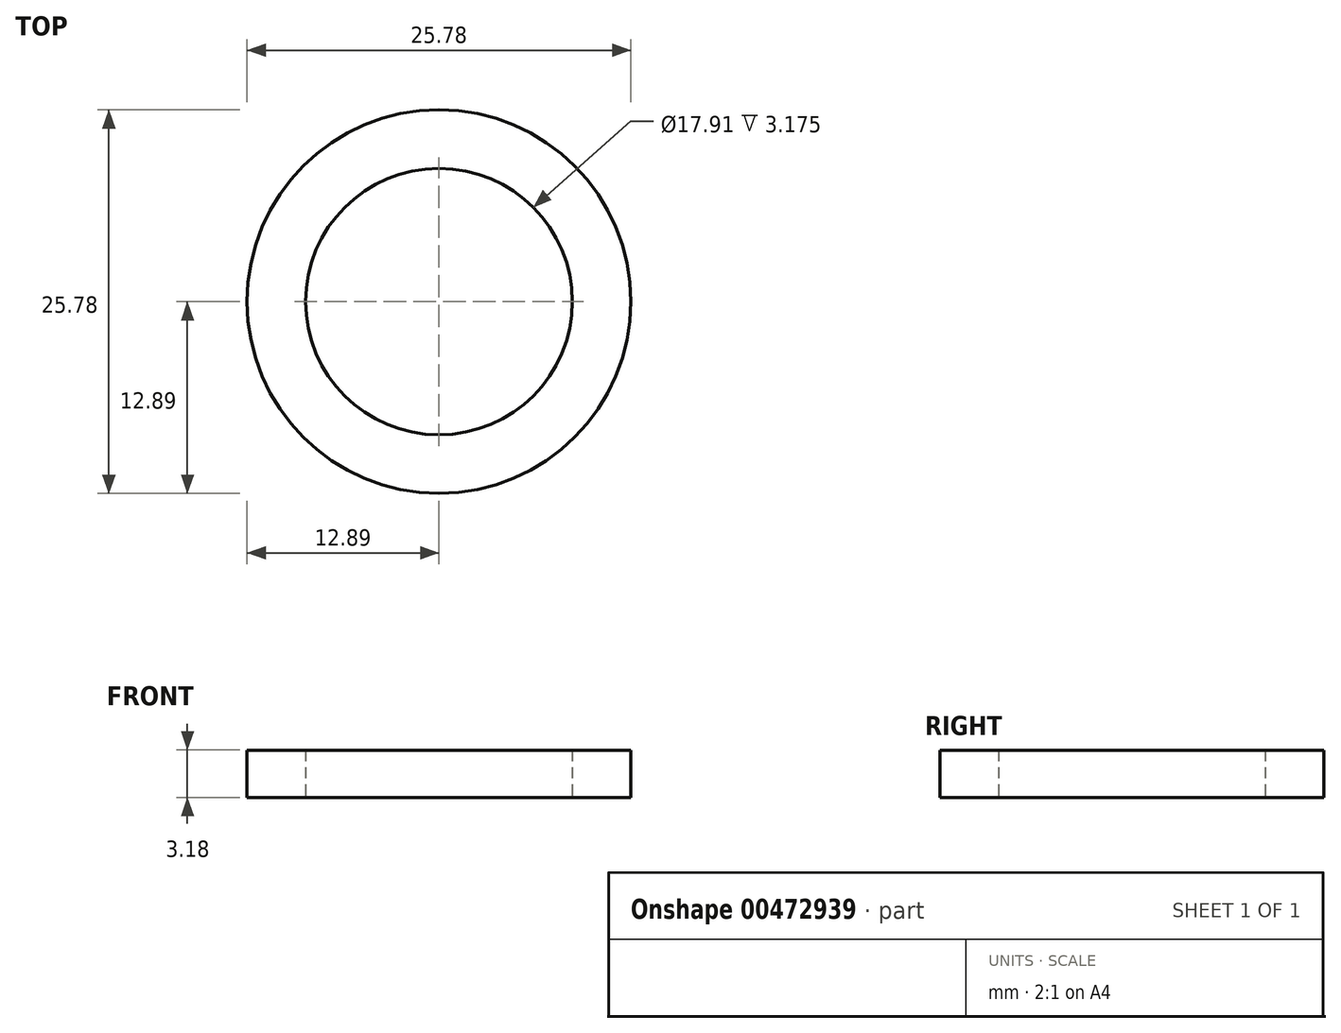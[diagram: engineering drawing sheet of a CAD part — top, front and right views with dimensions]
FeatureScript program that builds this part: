
annotation { "Feature Type Name" : "Feature", "Feature Type Description" : "" }
export const myFeature = defineFeature(function(context is Context, id is Id, definition is map)
    precondition{}
    {
        {
            var Q0;
            Q0=qCreatedBy(makeId("Top.planeOp"),FACE);
            var sketch = newSketch(context, id + "F0", { "sketchPlane" : qUnion([Q0])});
            skCircle(sketch, "E0", {"center": v(0, 0) * mm, "radius": 12.9 * mm});
            skCircle(sketch, "E1", {"center": v(0, 0) * mm, "radius": 8.95 * mm});
            skSolve(sketch);
        }
        {
            var Q0;
            Q0=makeQuery(id+"F0.imprint","IMPRINT",FACE,{"disambiguationData":[TD([[makeQuery(id+"F0.imprint","IMPRINT",EDGE,{"derivedFrom":sQuery(id+"F0.wireOp",EDGE,"E0")}),1.0]])]});
            extrude(context, id + "F1", {"entities" : qUnion([Q0]), "depth" : 3.17 * mm, "offsetDistance" : 25.4 * mm});
        }
    });
